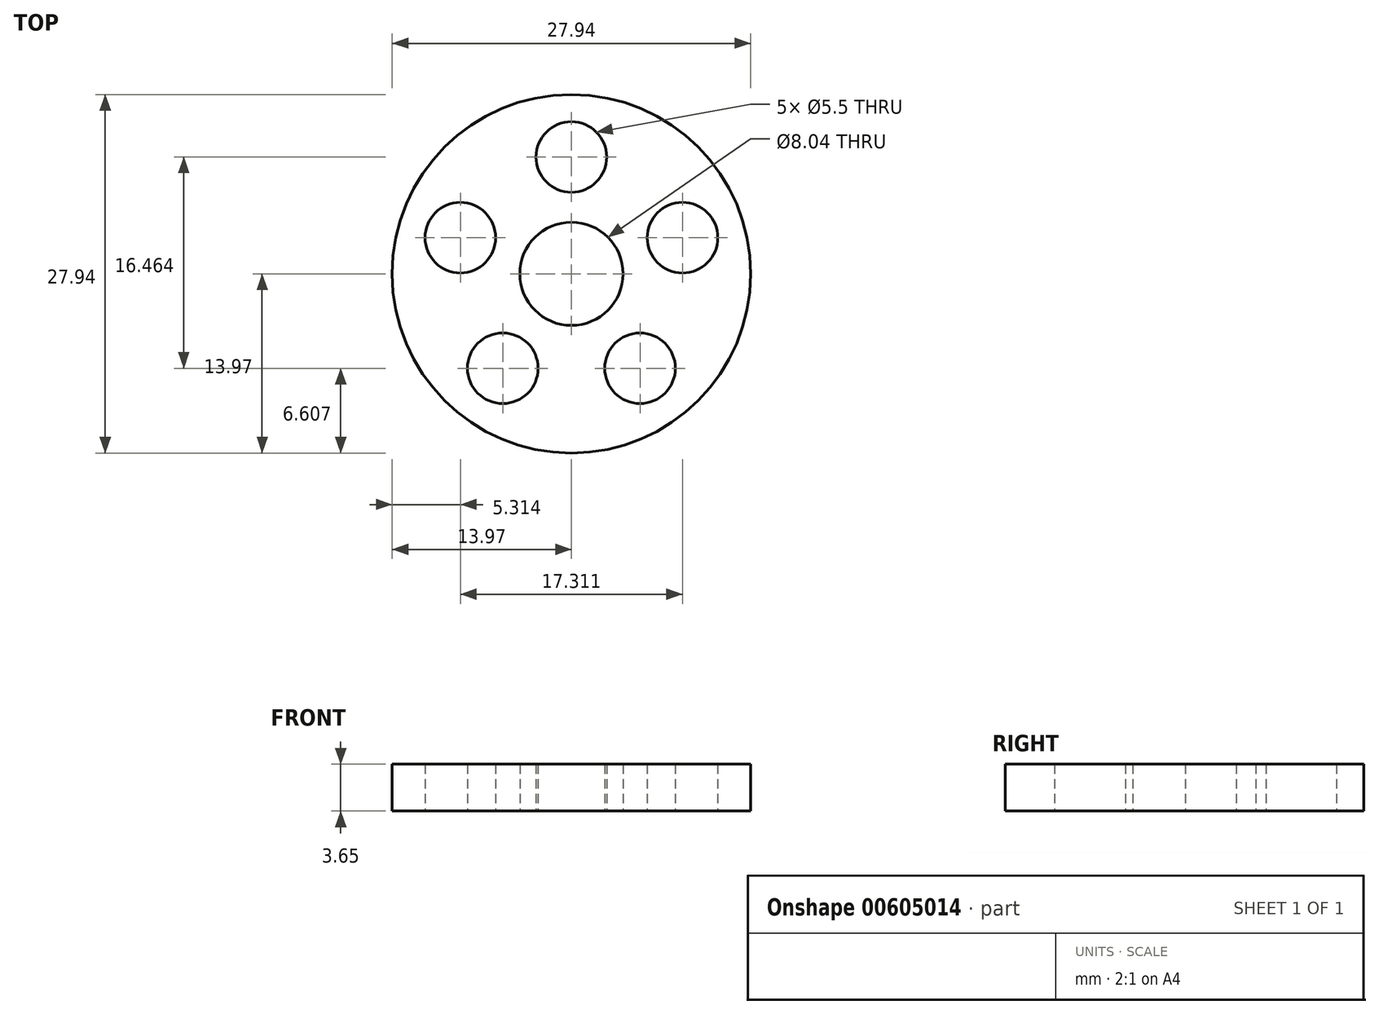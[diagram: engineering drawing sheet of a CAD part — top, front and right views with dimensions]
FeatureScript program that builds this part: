
annotation { "Feature Type Name" : "Feature", "Feature Type Description" : "" }
export const myFeature = defineFeature(function(context is Context, id is Id, definition is map)
    precondition{}
    {
        {
            var Q0;
            Q0=qCreatedBy(makeId("Top.planeOp"),FACE);
            var sketch = newSketch(context, id + "F0", { "sketchPlane" : qUnion([Q0])});
            skCircle(sketch, "E0", {"center": v(0, 0) * mm, "radius": 13.97 * mm});
            skCircle(sketch, "E1", {"center": v(0, 0) * mm, "radius": 4.02 * mm});
            skLineSegment(sketch, "E2", {"start": v(0, 0) * mm, "end": v(0, 9.1) * mm});
            skCircle(sketch, "E3", {"center": v(0, 9.1) * mm, "radius": 2.75 * mm});
            skCircle(sketch, "E4.1.0", {"center": v(-8.66, 2.81) * mm, "radius": 2.75 * mm});
            skCircle(sketch, "E4.2.0", {"center": v(-5.35, -7.36) * mm, "radius": 2.75 * mm});
            skCircle(sketch, "E4.3.0", {"center": v(5.35, -7.36) * mm, "radius": 2.75 * mm});
            skCircle(sketch, "E4.4.0", {"center": v(8.66, 2.81) * mm, "radius": 2.75 * mm});
            skSolve(sketch);
        }
        {
            var Q0;
            Q0=makeQuery(id+"F0.imprint","IMPRINT",FACE,{"disambiguationData":[TD([[makeQuery(id+"F0.imprint","IMPRINT",EDGE,{"derivedFrom":sQuery(id+"F0.wireOp",EDGE,"E1")}),-1.0]])]});
            extrude(context, id + "F1", {"entities" : qUnion([Q0]), "depth" : 3.65 * mm, "offsetDistance" : 25 * mm});
        }
    });
